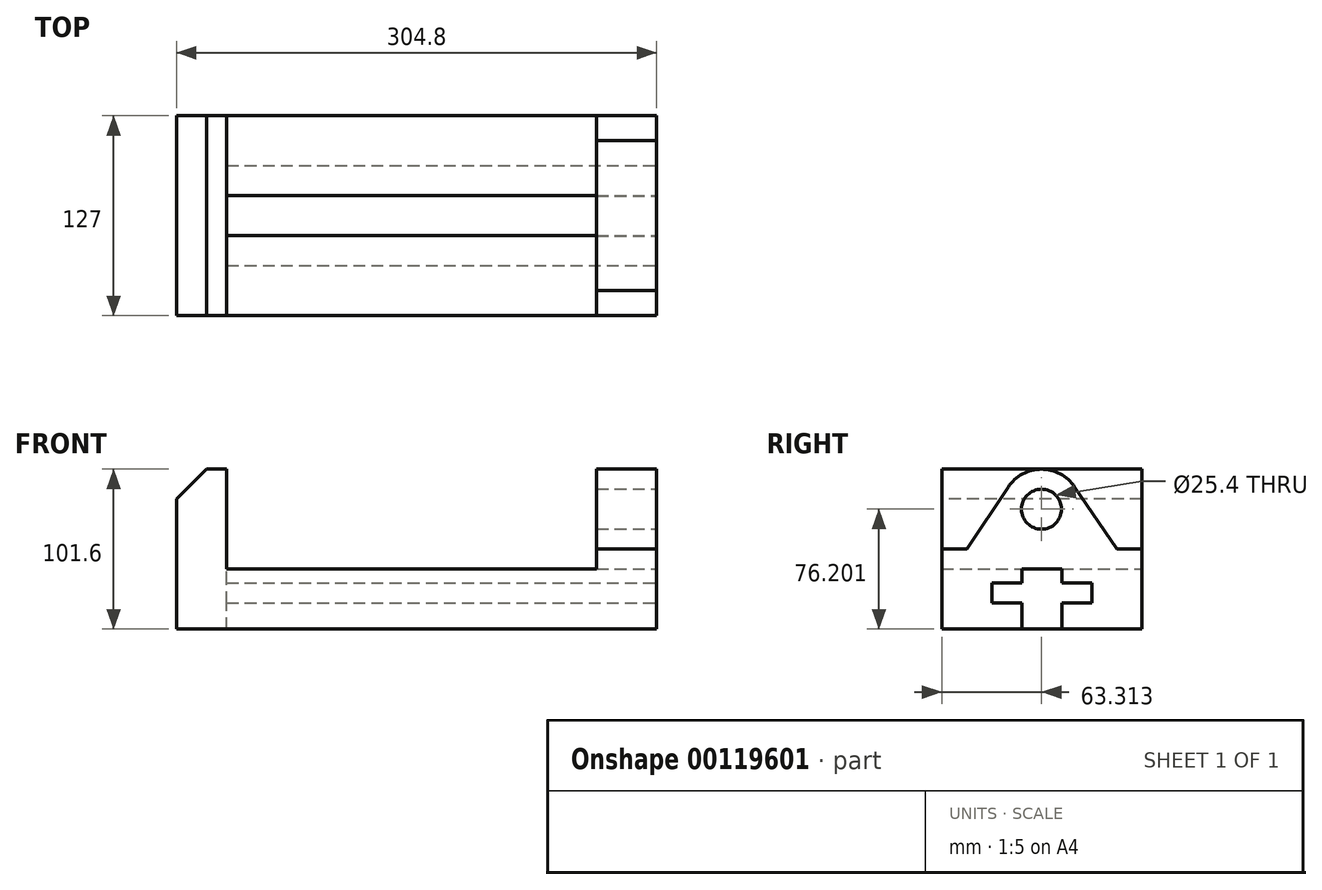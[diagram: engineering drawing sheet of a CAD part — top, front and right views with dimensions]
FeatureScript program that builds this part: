
annotation { "Feature Type Name" : "Feature", "Feature Type Description" : "" }
export const myFeature = defineFeature(function(context is Context, id is Id, definition is map)
    precondition{}
    {
        {
            var Q0;
            Q0=qCreatedBy(makeId("Top.planeOp"),FACE);
            var sketch = newSketch(context, id + "F0", { "sketchPlane" : qUnion([Q0])});
            skLineSegment(sketch, "E0.bottom", {"start": v(0, 0) * mm, "end": v(304.8, 0) * mm});
            skLineSegment(sketch, "E0.top", {"start": v(0, 127) * mm, "end": v(304.8, 127) * mm});
            skLineSegment(sketch, "E0.left", {"start": v(0, 0) * mm, "end": v(0, 127) * mm});
            skLineSegment(sketch, "E0.right", {"start": v(304.8, 0) * mm, "end": v(304.8, 127) * mm});
            skSolve(sketch);
        }
        {
            var Q0;
            Q0 = qSketchRegion(id + "F0", true);
            extrude(context, id + "F1", {"entities" : qUnion([Q0]), "depth" : 38.1 * mm});
        }
        {
            var Q0;
            Q0=makeQuery(id+"F1.opExtrude","CAP_FACE",FACE,{"disambiguationData":[OSD([sQuery(id+"F0.wireOp",EDGE,"E0.bottom"),sQuery(id+"F0.wireOp",EDGE,"E0.top"),sQuery(id+"F0.wireOp",EDGE,"E0.left"),sQuery(id+"F0.wireOp",EDGE,"E0.right")])],"isStart":false});
            var sketch = newSketch(context, id + "F2", { "sketchPlane" : qUnion([Q0])});
            skLineSegment(sketch, "E1", {"start": v(31.75, 127) * mm, "end": v(31.75, 0) * mm});
            skLineSegment(sketch, "E2", {"start": v(31.75, 127) * mm, "end": v(0, 127) * mm});
            skLineSegment(sketch, "E3", {"start": v(0, 127) * mm, "end": v(0, 0) * mm});
            skLineSegment(sketch, "E4", {"start": v(0, 0) * mm, "end": v(31.75, 0) * mm});
            skSolve(sketch);
        }
        {
            var Q0;
            Q0 = qSketchRegion(id + "F2", true);
            extrude(context, id + "F3", {"entities" : qUnion([Q0]), "operationType" : NewBodyOperationType.ADD, "depth" : 63.5 * mm});
        }
        {
            var Q0;
            Q0=makeQuery(id+"F3.boolean.opBoolean","MERGE",FACE,{"derivedFrom":[makeQuery(id+"F1.opExtrude","SWEPT_FACE",FACE,{"disambiguationData":[OSD([sQuery(id+"F0.wireOp",EDGE,"E0.bottom")])]}),makeQuery(id+"F3.opExtrude","SWEPT_FACE",FACE,{"disambiguationData":[OSD([sQuery(id+"F2.wireOp",EDGE,"E4")])]})]});
            var sketch = newSketch(context, id + "F4", { "sketchPlane" : qUnion([Q0])});
            skLineSegment(sketch, "E5", {"start": v(0, 101.6) * mm, "end": v(0, 82.55) * mm});
            skLineSegment(sketch, "E6", {"start": v(0, 82.55) * mm, "end": v(19.05, 101.6) * mm});
            skLineSegment(sketch, "E7", {"start": v(19.05, 101.6) * mm, "end": v(0, 101.6) * mm});
            skSolve(sketch);
        }
        {
            var Q0;
            Q0=makeQuery(id+"F4.imprint","IMPRINT",FACE,{"disambiguationData":[TD([[makeQuery(id+"F4.imprint","IMPRINT",EDGE,{"derivedFrom":sQuery(id+"F4.wireOp",EDGE,"E5")}),1.0]])]});
            extrude(context, id + "F5", {"entities" : qUnion([Q0]), "operationType" : NewBodyOperationType.REMOVE, "endBound" : BoundingType.THROUGH_ALL, "oppositeDirection" : true, "depth" : 25.4 * mm});
        }
        {
            var Q0;
            Q0=makeQuery(id+"F1.opExtrude","SWEPT_FACE",FACE,{"disambiguationData":[OSD([sQuery(id+"F0.wireOp",EDGE,"E0.right")])]});
            var sketch = newSketch(context, id + "F6", { "sketchPlane" : qUnion([Q0])});
            skLineSegment(sketch, "E8", {"start": v(50.8, 0) * mm, "end": v(50.8, 16.51) * mm});
            skLineSegment(sketch, "E9", {"start": v(50.8, 16.51) * mm, "end": v(31.75, 16.51) * mm});
            skLineSegment(sketch, "E10", {"start": v(31.75, 16.51) * mm, "end": v(31.75, 29.21) * mm});
            skLineSegment(sketch, "E11", {"start": v(31.75, 29.21) * mm, "end": v(50.8, 29.21) * mm});
            skLineSegment(sketch, "E12", {"start": v(50.8, 29.2) * mm, "end": v(50.8, 38.1) * mm});
            skLineSegment(sketch, "E13", {"start": v(50.8, 38.1) * mm, "end": v(76.2, 38.1) * mm});
            skLineSegment(sketch, "E14", {"start": v(76.2, 38.1) * mm, "end": v(76.2, 29.2) * mm});
            skLineSegment(sketch, "E15", {"start": v(76.2, 29.2) * mm, "end": v(95.25, 29.21) * mm});
            skLineSegment(sketch, "E16", {"start": v(95.25, 29.21) * mm, "end": v(95.25, 16.51) * mm});
            skLineSegment(sketch, "E17", {"start": v(95.25, 16.51) * mm, "end": v(76.2, 16.51) * mm});
            skLineSegment(sketch, "E18", {"start": v(76.2, 16.51) * mm, "end": v(76.2, 0) * mm});
            skSolve(sketch);
        }
        {
            var Q0;
            Q0 = qSketchRegion(id + "F6", true);
            var Q1;
            {var subQ0=sQuery(id+"F6.wireOp",EDGE,"E8");Q1=makeQuery(id+"F6.imprint","IMPRINT",FACE,{"disambiguationData":[TD([[makeQuery(id+"F6.imprint","IMPRINT",EDGE,{"derivedFrom":subQ0}),-1.0]])]});}
            extrude(context, id + "F7", {"entities" : qUnion([Q0, Q1]), "operationType" : NewBodyOperationType.REMOVE, "oppositeDirection" : true, "depth" : 273.05 * mm});
        }
        {
            var Q0;
            {var subQ0=sQuery(id+"F0.wireOp",EDGE,"E0.right");var subQ3=sQuery(id+"F0.wireOp",EDGE,"E0.bottom");Q0=makeQuery(id+"F7.boolean.opBoolean","SPLIT",FACE,{"disambiguationData":[TD([makeQuery(id+"F1.opExtrude","SWEPT_FACE",FACE,{"disambiguationData":[OSD([subQ3])]})])],"derivedFrom":makeQuery(id+"F1.opExtrude","SWEPT_FACE",FACE,{"disambiguationData":[OSD([subQ0])]})});}
            var sketch = newSketch(context, id + "F8", { "sketchPlane" : qUnion([Q0])});
            skLineSegment(sketch, "E19", {"start": v(0, 38.1) * mm, "end": v(0, 50.8) * mm});
            skLineSegment(sketch, "E20", {"start": v(0, 50.8) * mm, "end": v(15.88, 50.8) * mm});
            skLineSegment(sketch, "E21", {"start": v(127, 38.1) * mm, "end": v(127, 50.8) * mm});
            skLineSegment(sketch, "E22", {"start": v(127, 50.8) * mm, "end": v(111.13, 50.8) * mm});
            skLineSegment(sketch, "E23", {"start": v(0, 0) * mm, "end": v(63.5, 0) * mm, "construction": true});
            skPoint(sketch, "E23.endSnap0", {"position": v(25.4, 0) * mm});
            skLineSegment(sketch, "E24", {"start": v(63.5, 0) * mm, "end": v(63.5, 101.6) * mm, "construction": true});
            skPoint(sketch, "E25.visualSharp", {"position": v(63.5, 101.6) * mm});
            skLineSegment(sketch, "E26", {"start": v(15.88, 50.8) * mm, "end": v(42.17, 90.28) * mm});
            skLineSegment(sketch, "E27", {"start": v(111.13, 50.8) * mm, "end": v(84.36, 90.42) * mm});
            skArc(sketch, "E28", {"start": v(84.36, 90.42) * mm, "mid": v(63.23, 101.6) * mm, "end": v(42.17, 90.28) * mm});
            skLineSegment(sketch, "E29", {"start": v(0, 38.1) * mm, "end": v(127, 38.1) * mm});
            skSolve(sketch);
        }
        {
            var Q0;
            Q0 = qSketchRegion(id + "F8", true);
            extrude(context, id + "F9", {"entities" : qUnion([Q0]), "operationType" : NewBodyOperationType.ADD, "oppositeDirection" : true, "depth" : 38.1 * mm});
        }
        {
            var Q0;
            {var subQ0=sQuery(id+"F0.wireOp",EDGE,"E0.top");var subQ1=sQuery(id+"F0.wireOp",EDGE,"E0.right");var subQ3=sQuery(id+"F0.wireOp",EDGE,"E0.bottom");var subQ6=makeQuery(id+"F1.opExtrude","SWEPT_FACE",FACE,{"disambiguationData":[OSD([subQ1])]});Q0=makeQuery(id+"F9.boolean.opBoolean","MERGE",FACE,{"derivedFrom":[makeQuery(id+"F7.boolean.opBoolean","SPLIT",FACE,{"disambiguationData":[TD([makeQuery(id+"F1.opExtrude","SWEPT_FACE",FACE,{"disambiguationData":[OSD([subQ3])]})])],"derivedFrom":subQ6}),makeQuery(id+"F7.boolean.opBoolean","SPLIT",FACE,{"disambiguationData":[TD([makeQuery(id+"F1.opExtrude","SWEPT_FACE",FACE,{"disambiguationData":[OSD([subQ0])]})])],"derivedFrom":subQ6}),makeQuery(id+"F9.opExtrude","CAP_FACE",FACE,{"disambiguationData":[OSD([sQuery(id+"F8.wireOp",EDGE,"E19"),sQuery(id+"F8.wireOp",EDGE,"E20"),sQuery(id+"F8.wireOp",EDGE,"E21"),sQuery(id+"F8.wireOp",EDGE,"E22"),sQuery(id+"F8.wireOp",EDGE,"E26"),sQuery(id+"F8.wireOp",EDGE,"E27"),sQuery(id+"F8.wireOp",EDGE,"E28"),sQuery(id+"F8.wireOp",EDGE,"E29")])],"isStart":true})]});}
            var sketch = newSketch(context, id + "F10", { "sketchPlane" : qUnion([Q0])});
            skLineSegment(sketch, "E30", {"start": v(0, 0) * mm, "end": v(63.5, 0) * mm, "construction": true});
            skLineSegment(sketch, "E31", {"start": v(63.5, 0) * mm, "end": v(63.5, 101.6) * mm, "construction": true});
            skCircle(sketch, "E32", {"center": v(63.31, 76.2) * mm, "radius": 12.7 * mm});
            skSolve(sketch);
        }
        {
            var Q0;
            Q0 = qSketchRegion(id + "F10", true);
            extrude(context, id + "F11", {"entities" : qUnion([Q0]), "operationType" : NewBodyOperationType.REMOVE, "oppositeDirection" : true, "depth" : 38.1 * mm});
        }
    });
